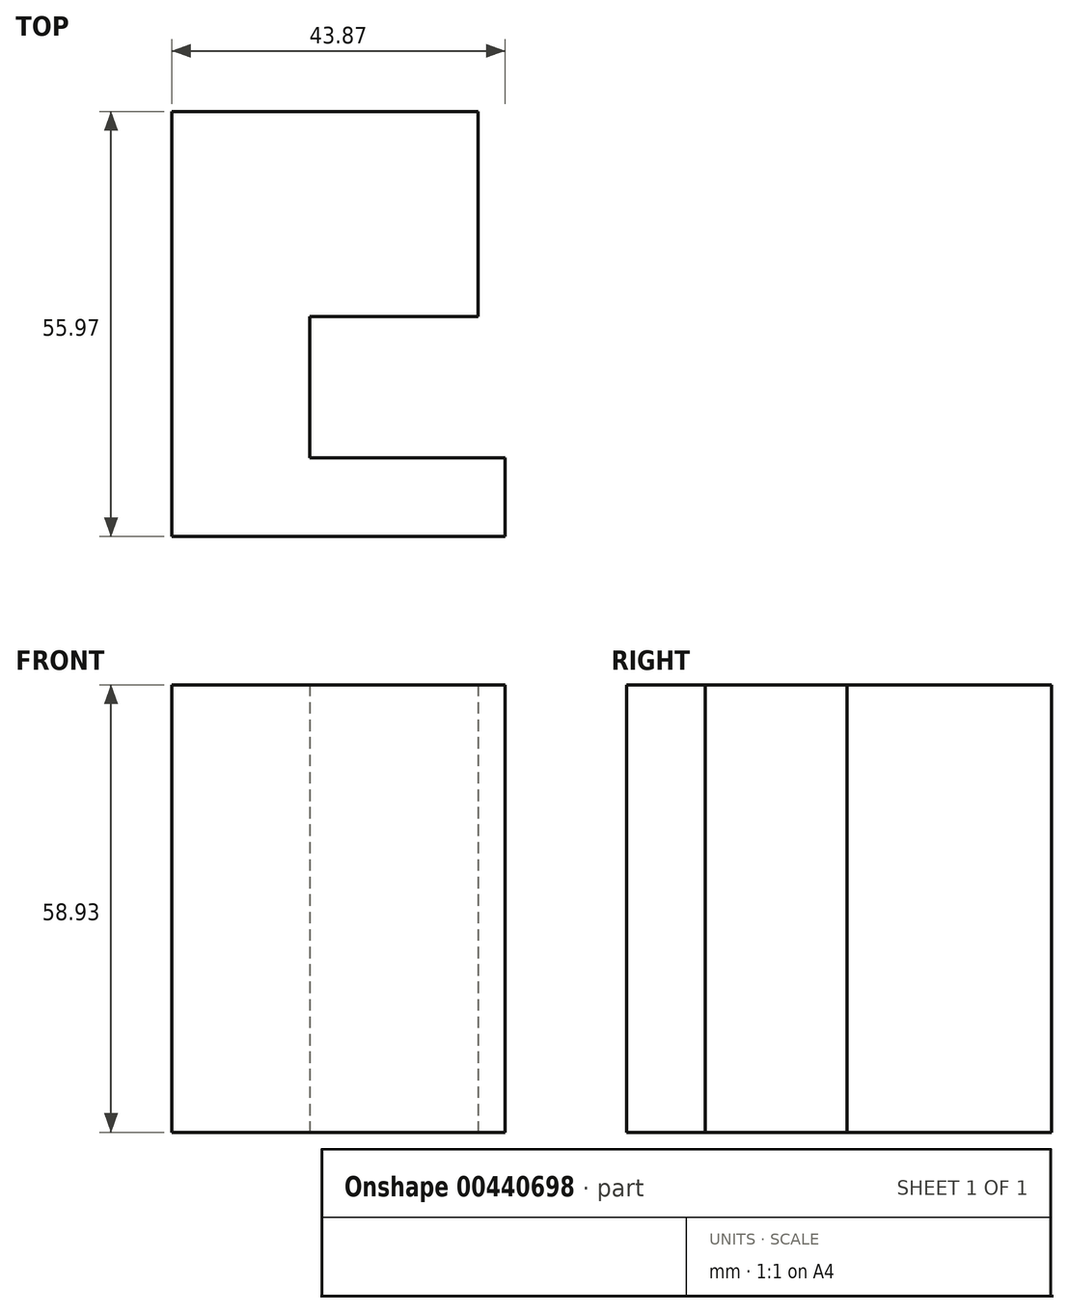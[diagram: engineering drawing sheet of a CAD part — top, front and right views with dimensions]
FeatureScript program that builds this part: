
annotation { "Feature Type Name" : "Feature", "Feature Type Description" : "" }
export const myFeature = defineFeature(function(context is Context, id is Id, definition is map)
    precondition{}
    {
        {
            var Q0;
            Q0=qCreatedBy(makeId("Top.planeOp"),FACE);
            var sketch = newSketch(context, id + "F0", { "sketchPlane" : qUnion([Q0])});
            skLineSegment(sketch, "E0", {"start": v(0, 0) * mm, "end": v(0, 55.97) * mm});
            skLineSegment(sketch, "E1", {"start": v(0, 55.97) * mm, "end": v(40.3, 55.97) * mm});
            skLineSegment(sketch, "E2", {"start": v(40.3, 55.97) * mm, "end": v(40.3, 29) * mm});
            skLineSegment(sketch, "E3", {"start": v(40.3, 29) * mm, "end": v(18.18, 29) * mm});
            skLineSegment(sketch, "E4", {"start": v(18.18, 29) * mm, "end": v(18.18, 10.36) * mm});
            skLineSegment(sketch, "E5", {"start": v(18.18, 10.36) * mm, "end": v(43.87, 10.36) * mm});
            skLineSegment(sketch, "E6", {"start": v(43.87, 10.36) * mm, "end": v(43.87, 0) * mm});
            skLineSegment(sketch, "E7", {"start": v(43.87, 0) * mm, "end": v(0, 0) * mm});
            skSolve(sketch);
        }
        {
            var Q0;
            Q0=makeQuery(id+"F0.imprint","IMPRINT",FACE,{"disambiguationData":[TD([[makeQuery(id+"F0.imprint","IMPRINT",EDGE,{"derivedFrom":sQuery(id+"F0.wireOp",EDGE,"E0")}),-1.0]])]});
            extrude(context, id + "F1", {"entities" : qUnion([Q0]), "depth" : 58.93 * mm});
        }
    });
